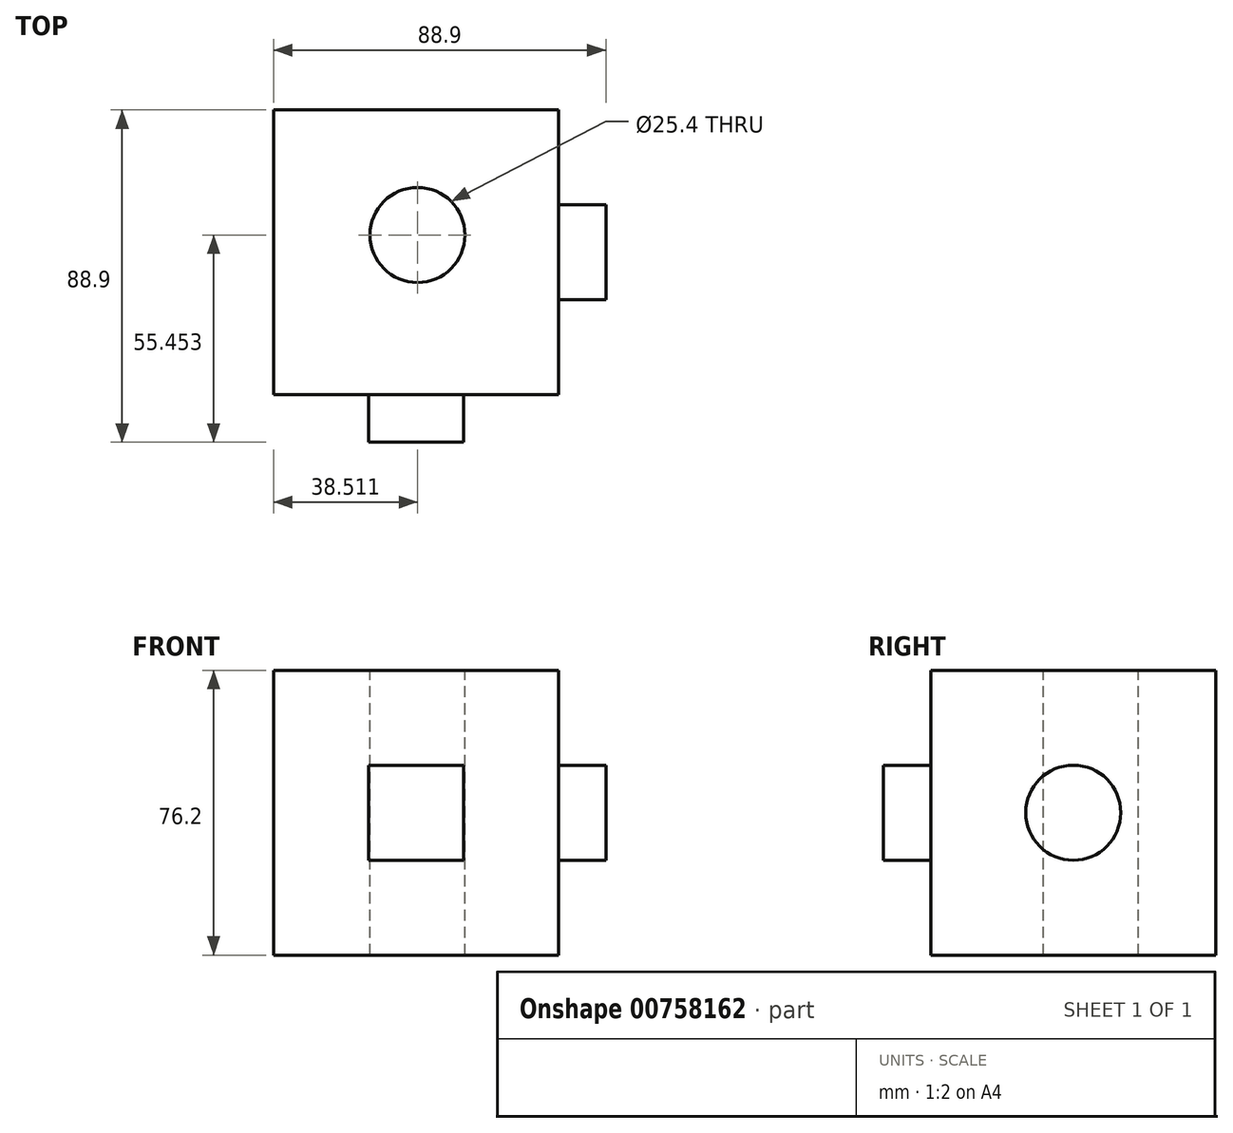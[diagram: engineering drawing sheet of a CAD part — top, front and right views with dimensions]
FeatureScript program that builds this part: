
annotation { "Feature Type Name" : "Feature", "Feature Type Description" : "" }
export const myFeature = defineFeature(function(context is Context, id is Id, definition is map)
    precondition{}
    {
        {
            var Q0;
            Q0=qCreatedBy(makeId("Front.planeOp"),FACE);
            var sketch = newSketch(context, id + "F0", { "sketchPlane" : qUnion([Q0])});
            skLineSegment(sketch, "E0.bottom", {"start": v(0, 0) * mm, "end": v(76.2, 0) * mm});
            skLineSegment(sketch, "E0.top", {"start": v(0, 76.2) * mm, "end": v(76.2, 76.2) * mm});
            skLineSegment(sketch, "E0.left", {"start": v(0, 0) * mm, "end": v(0, 76.2) * mm});
            skLineSegment(sketch, "E0.right", {"start": v(76.2, 0) * mm, "end": v(76.2, 76.2) * mm});
            skSolve(sketch);
        }
        {
            var Q0;
            Q0=makeQuery(id+"F0.imprint","IMPRINT",FACE,{"disambiguationData":[TD([[makeQuery(id+"F0.imprint","IMPRINT",EDGE,{"derivedFrom":sQuery(id+"F0.wireOp",EDGE,"E0.bottom")}),1.0]])]});
            extrude(context, id + "F1", {"entities" : qUnion([Q0]), "depth" : 76.2 * mm, "offsetDistance" : 25.4 * mm});
        }
        {
            var Q0;
            Q0=makeQuery(id+"F1.opExtrude","SWEPT_FACE",FACE,{"disambiguationData":[OSD([sQuery(id+"F0.wireOp",EDGE,"E0.top")])]});
            var sketch = newSketch(context, id + "F2", { "sketchPlane" : qUnion([Q0])});
            skPoint(sketch, "E1", {"position": v(38.51, -33.45) * mm});
            skPoint(sketch, "E2", {"position": v(-52.39, -61.15) * mm});
            skSolve(sketch);
        }
        {
            var Q0;
            Q0=sQuery(id+"F2.wireOp",VERTEX,"E1");
            var Q1;
            Q1=makeQuery(id+"F1.opExtrude","SWEPT_BODY",BODY,{"disambiguationData":[OSD([sQuery(id+"F0.wireOp",EDGE,"E0.bottom"),sQuery(id+"F0.wireOp",EDGE,"E0.top"),sQuery(id+"F0.wireOp",EDGE,"E0.left"),sQuery(id+"F0.wireOp",EDGE,"E0.right")])]});
            hole(context, id + "F3", {"style" : HoleStyle.SIMPLE, "endStyle" : HoleEndStyle.THROUGH, "holeDiameter" : 25.4 * mm, "majorDiameter" : 6.35 * mm, "isTappedThrough" : true, "tappedDepth" : 12.7 * mm, "tapClearance" : 3, "locations" : qUnion([Q0]), "scope" : qUnion([Q1])});
        }
        {
            var Q0;
            Q0=makeQuery(id+"F1.opExtrude","CAP_FACE",FACE,{"disambiguationData":[OSD([sQuery(id+"F0.wireOp",EDGE,"E0.bottom"),sQuery(id+"F0.wireOp",EDGE,"E0.top"),sQuery(id+"F0.wireOp",EDGE,"E0.left"),sQuery(id+"F0.wireOp",EDGE,"E0.right")])],"isStart":false});
            var sketch = newSketch(context, id + "F4", { "sketchPlane" : qUnion([Q0])});
            skPoint(sketch, "E3", {"position": v(38.1, 38.1) * mm});
            skLineSegment(sketch, "E4.bottom", {"start": v(50.8, 50.8) * mm, "end": v(25.4, 50.8) * mm});
            skLineSegment(sketch, "E4.top", {"start": v(50.8, 25.4) * mm, "end": v(25.4, 25.4) * mm});
            skLineSegment(sketch, "E4.left", {"start": v(50.8, 50.8) * mm, "end": v(50.8, 25.4) * mm});
            skLineSegment(sketch, "E4.right", {"start": v(25.4, 50.8) * mm, "end": v(25.4, 25.4) * mm});
            skSolve(sketch);
        }
        {
            var Q0;
            Q0 = qSketchRegion(id + "F4", true);
            extrude(context, id + "F5", {"entities" : qUnion([Q0]), "operationType" : NewBodyOperationType.ADD, "depth" : 12.7 * mm, "offsetDistance" : 25.4 * mm});
        }
        {
            var Q0;
            Q0=makeQuery(id+"F1.opExtrude","SWEPT_FACE",FACE,{"disambiguationData":[OSD([sQuery(id+"F0.wireOp",EDGE,"E0.right")])]});
            var sketch = newSketch(context, id + "F6", { "sketchPlane" : qUnion([Q0])});
            skPoint(sketch, "E5", {"position": v(-38.1, 38.1) * mm});
            skCircle(sketch, "E6", {"center": v(-38.1, 38.1) * mm, "radius": 12.7 * mm});
            skSolve(sketch);
        }
        {
            var Q0;
            Q0 = qSketchRegion(id + "F6", true);
            extrude(context, id + "F7", {"entities" : qUnion([Q0]), "operationType" : NewBodyOperationType.ADD, "depth" : 12.7 * mm, "offsetDistance" : 25.4 * mm});
        }
    });
